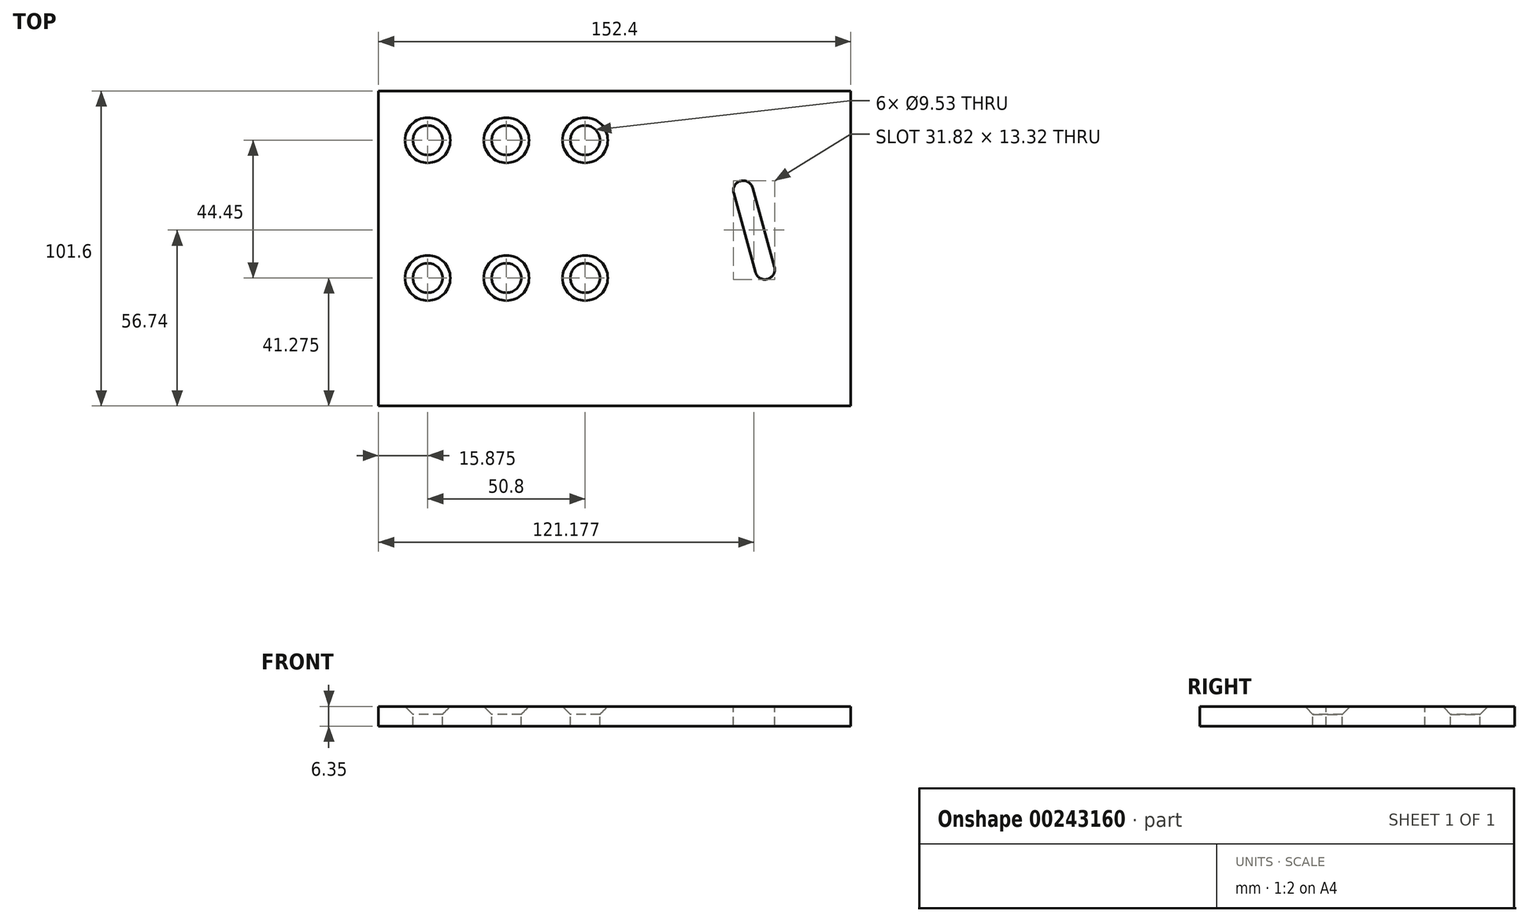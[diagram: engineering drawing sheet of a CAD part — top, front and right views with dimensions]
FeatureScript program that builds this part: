
annotation { "Feature Type Name" : "Feature", "Feature Type Description" : "" }
export const myFeature = defineFeature(function(context is Context, id is Id, definition is map)
    precondition{}
    {
        {
            var Q0;
            Q0=qCreatedBy(makeId("Top.planeOp"),FACE);
            var sketch = newSketch(context, id + "F0", { "sketchPlane" : qUnion([Q0])});
            skLineSegment(sketch, "E0.bottom", {"start": v(76.2, 50.8) * mm, "end": v(-76.2, 50.8) * mm});
            skLineSegment(sketch, "E0.top", {"start": v(76.2, -50.8) * mm, "end": v(-76.2, -50.8) * mm});
            skLineSegment(sketch, "E0.left", {"start": v(76.2, 50.8) * mm, "end": v(76.2, -50.8) * mm});
            skLineSegment(sketch, "E0.right", {"start": v(-76.2, 50.8) * mm, "end": v(-76.2, -50.8) * mm});
            skPoint(sketch, "E0.middle", {"position": v(0, 0) * mm});
            skCircle(sketch, "E1", {"center": v(-60.33, 34.93) * mm, "radius": 4.76 * mm});
            skCircle(sketch, "E2.0.1.0", {"center": v(-60.33, -9.52) * mm, "radius": 4.76 * mm});
            skCircle(sketch, "E2.1.0.0", {"center": v(-34.93, 34.93) * mm, "radius": 4.76 * mm});
            skCircle(sketch, "E2.1.1.0", {"center": v(-34.93, -9.52) * mm, "radius": 4.76 * mm});
            skCircle(sketch, "E2.2.0.0", {"center": v(-9.53, 34.93) * mm, "radius": 4.76 * mm});
            skCircle(sketch, "E2.2.1.0", {"center": v(-9.53, -9.52) * mm, "radius": 4.76 * mm});
            skLineSegment(sketch, "E2.direction1", {"start": v(-60.33, 34.93) * mm, "end": v(-34.93, 34.93) * mm, "construction": true});
            skLineSegment(sketch, "E2.direction2", {"start": v(-60.33, 34.93) * mm, "end": v(-60.33, -9.52) * mm, "construction": true});
            skSolve(sketch);
        }
        {
            var Q0;
            Q0=makeQuery(id+"F0.imprint","IMPRINT",FACE,{"disambiguationData":[TD([[makeQuery(id+"F0.imprint","IMPRINT",EDGE,{"derivedFrom":sQuery(id+"F0.wireOp",EDGE,"E0.bottom")}),1.0]])]});
            var sketch = newSketch(context, id + "F1", { "sketchPlane" : qUnion([Q0])});
            skArc(sketch, "E3", {"start": v(44.53, 19.54) * mm, "mid": v(40.63, 21.76) * mm, "end": v(38.4, 17.86) * mm});
            skArc(sketch, "E4", {"start": v(45.42, -7.66) * mm, "mid": v(49.33, -9.88) * mm, "end": v(51.55, -5.98) * mm});
            skLineSegment(sketch, "E5", {"start": v(45.42, -7.66) * mm, "end": v(38.4, 17.86) * mm});
            skLineSegment(sketch, "E6", {"start": v(44.53, 19.54) * mm, "end": v(51.55, -5.98) * mm});
            skSolve(sketch);
        }
        {
            var Q0;
            Q0=makeQuery(id+"F0.imprint","IMPRINT",FACE,{"disambiguationData":[TD([[makeQuery(id+"F0.imprint","IMPRINT",EDGE,{"derivedFrom":sQuery(id+"F0.wireOp",EDGE,"E0.bottom")}),1.0]])]});
            extrude(context, id + "F2", {"entities" : qUnion([Q0]), "oppositeDirection" : true, "depth" : 6.35 * mm});
        }
        {
            var Q0;
            Q0=makeQuery(id+"F1.imprint","IMPRINT",FACE,{"disambiguationData":[TD([[makeQuery(id+"F1.imprint","IMPRINT",EDGE,{"derivedFrom":sQuery(id+"F1.wireOp",EDGE,"E3")}),1.0]])]});
            extrude(context, id + "F3", {"entities" : qUnion([Q0]), "operationType" : NewBodyOperationType.REMOVE, "oppositeDirection" : true, "depth" : 25.4 * mm});
        }
        {
            var Q0;
            Q0=makeQuery(id+"F2.opExtrude","CAP_EDGE",EDGE,{"disambiguationData":[OSD([sQuery(id+"F0.wireOp",EDGE,"E1")])],"isStart":true});
            var Q1;
            Q1=makeQuery(id+"F2.opExtrude","CAP_EDGE",EDGE,{"disambiguationData":[OSD([sQuery(id+"F0.wireOp",EDGE,"E2.1.0.0")])],"isStart":true});
            var Q2;
            Q2=makeQuery(id+"F2.opExtrude","CAP_EDGE",EDGE,{"disambiguationData":[OSD([sQuery(id+"F0.wireOp",EDGE,"E2.2.0.0")])],"isStart":true});
            var Q3;
            Q3=makeQuery(id+"F2.opExtrude","CAP_EDGE",EDGE,{"disambiguationData":[OSD([sQuery(id+"F0.wireOp",EDGE,"E2.2.1.0")])],"isStart":true});
            var Q4;
            Q4=makeQuery(id+"F2.opExtrude","CAP_EDGE",EDGE,{"disambiguationData":[OSD([sQuery(id+"F0.wireOp",EDGE,"E2.1.1.0")])],"isStart":true});
            var Q5;
            Q5=makeQuery(id+"F2.opExtrude","CAP_EDGE",EDGE,{"disambiguationData":[OSD([sQuery(id+"F0.wireOp",EDGE,"E2.0.1.0")])],"isStart":true});
            var Q6;
            Q6=makeQuery(id+"F3.boolean.opBoolean","COPY",EDGE,{"derivedFrom":makeQuery(id+"F3.opExtrude","CAP_EDGE",EDGE,{"disambiguationData":[OSD([sQuery(id+"F1.wireOp",EDGE,"E5")])],"isStart":true})});
            chamfer(context, id + "F4", {"entities" : qUnion([Q0, Q1, Q2, Q3, Q4, Q5, Q6]), "width" : 2.54 * mm, "tangentPropagation" : true});
        }
    });
